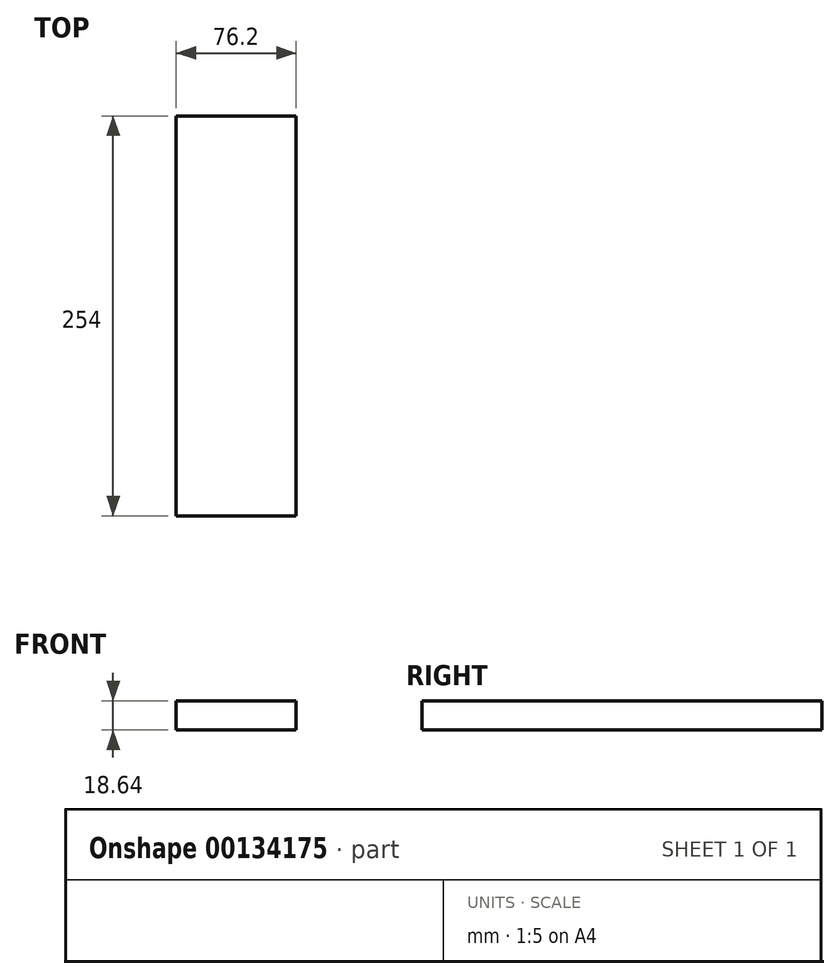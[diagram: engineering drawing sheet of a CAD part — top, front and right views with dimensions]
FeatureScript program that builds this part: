
annotation { "Feature Type Name" : "Feature", "Feature Type Description" : "" }
export const myFeature = defineFeature(function(context is Context, id is Id, definition is map)
    precondition{}
    {
        {
            var Q0;
            Q0=qCreatedBy(makeId("Front.planeOp"),FACE);
            var sketch = newSketch(context, id + "F0", { "sketchPlane" : qUnion([Q0])});
            skLineSegment(sketch, "E0.bottom", {"start": v(0, 0) * mm, "end": v(76.2, 0) * mm});
            skLineSegment(sketch, "E0.top", {"start": v(0, 18.64) * mm, "end": v(76.2, 18.64) * mm});
            skLineSegment(sketch, "E0.left", {"start": v(0, 0) * mm, "end": v(0, 18.64) * mm});
            skLineSegment(sketch, "E0.right", {"start": v(76.2, 0) * mm, "end": v(76.2, 18.64) * mm});
            skSolve(sketch);
        }
        {
            var Q0;
            Q0 = qSketchRegion(id + "F0", true);
            extrude(context, id + "F1", {"entities" : qUnion([Q0]), "depth" : 254 * mm});
        }
    });
